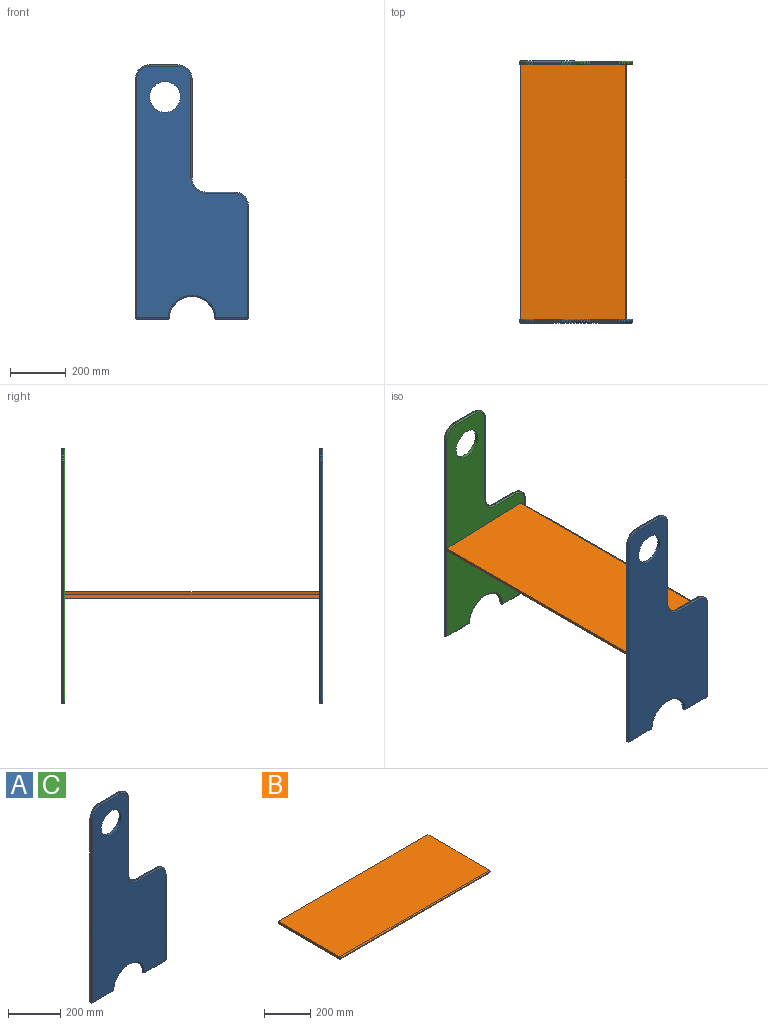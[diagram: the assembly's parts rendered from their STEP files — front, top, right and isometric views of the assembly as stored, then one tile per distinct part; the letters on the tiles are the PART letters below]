
ASSEMBLY  parts=3 mates=1
PART A: 51 faces, bbox 414.8x12.7x918.6 mm
  f0: plane 355.6x2.54mm, normal (1,0,0), area 903.2mm2, adj f10,f13,f19,f40
  f1: plane 101.6x2.54mm, normal (0,0,1), area 258.1mm2, adj f10,f11,f15,f31
  f2: plane 858.52x2.54mm, normal (-1,0,0), area 2180.6mm2, adj f11,f16,f21,f22
  f3: plane 111.61x2.54mm, normal (0,0,-1), area 283.5mm2, adj f20,f21,f29,f30
  f4: cylinder r=81.58mm len=162.87mm, axis (0,1,0), area 626.6mm2, adj f28,f29,f38,f39
  f5: plane 111.61x2.54mm, normal (0,0,-1), area 283.5mm2, adj f37,f38,f44,f45
  f6: plane 401.32x2.54mm, normal (1,0,0), area 1019.4mm2, adj f12,f36,f44,f49
  f7: plane 101.6x2.54mm, normal (0,0,1), area 258.1mm2, adj f12,f13,f27,f46
  f8: plane 904.24x396.24mm, normal (0,-1,0), area 244295.3mm2, adj f22,f26,f30,f31,f35,f39,f40,f43
  f9: plane 904.24x396.24mm, normal (0,1,0), area 244295.3mm2, adj f14,f15,f16,f17,f19,f20,f23,f27
  f10: cylinder r=50.8mm len=50.8mm, axis (0,1,0), area 202.7mm2, adj f0,f1,f17,f35
  f11: cylinder r=50.8mm len=50.8mm, axis (0,1,0), area 202.7mm2, adj f1,f2,f14,f26
  f12: cylinder r=50.8mm len=50.8mm, axis (0,1,0), area 202.7mm2, adj f6,f7,f32,f48
  f13: cylinder r=50.8mm len=50.8mm, axis (0,1,0), area 202.7mm2, adj f0,f7,f23,f43
  f14: torus R=45.72mm, axis (0,-1,0), area 613.6mm2, adj f9,f11,f15,f16
  f15: cylinder r=5.08mm len=101.6mm, axis (-1,0,0), area 810.7mm2, adj f1,f9,f14,f17
  f16: cylinder r=5.08mm len=858.52mm, axis (0,0,-1), area 6850.7mm2, adj f2,f9,f14,f18
  f17: torus R=45.72mm, axis (0,-1,0), area 613.6mm2, adj f9,f10,f15,f19
  f18: sphere r=5.08mm, area 40.5mm2, adj f16,f20,f21
  f19: cylinder r=5.08mm len=355.6mm, axis (0,0,1), area 2837.6mm2, adj f0,f9,f17,f23
  f20: cylinder r=5.08mm len=111.61mm, axis (1,0,0), area 890.6mm2, adj f3,f9,f18,f24
  f21: cylinder r=5.08mm len=5.08mm, axis (0,-1,0), area 20.3mm2, adj f2,f3,f18,f25
  f22: cylinder r=5.08mm len=858.52mm, axis (0,0,1), area 6850.7mm2, adj f2,f8,f25,f26
  f23: torus R=55.88mm, axis (0,-1,0), area 659.9mm2, adj f9,f13,f19,f27
  f24: sphere r=5.08mm, area 39mm2, adj f20,f28,f29
  f25: sphere r=5.08mm, area 40.5mm2, adj f21,f22,f30
  f26: torus R=45.72mm, axis (0,-1,0), area 613.6mm2, adj f8,f11,f22,f31
  f27: cylinder r=5.08mm len=101.6mm, axis (-1,0,0), area 810.7mm2, adj f7,f9,f23,f32
  f28: torus R=86.66mm, axis (0,-1,0), area 2013.2mm2, adj f4,f9,f24,f33
  f29: cylinder r=5.08mm len=5.07mm, axis (0,1,0), area 19.5mm2, adj f3,f4,f24,f34
  f30: cylinder r=5.08mm len=111.61mm, axis (-1,0,0), area 890.6mm2, adj f3,f8,f25,f34
  f31: cylinder r=5.08mm len=101.6mm, axis (1,0,0), area 810.7mm2, adj f1,f8,f26,f35
  f32: torus R=45.72mm, axis (0,-1,0), area 613.6mm2, adj f9,f12,f27,f36
  f33: sphere r=5.08mm, area 39mm2, adj f28,f37,f38
  f34: sphere r=5.08mm, area 39mm2, adj f29,f30,f39
  f35: torus R=45.72mm, axis (0,-1,0), area 613.6mm2, adj f8,f10,f31,f40
  f36: cylinder r=5.08mm len=401.32mm, axis (0,0,1), area 3202.4mm2, adj f6,f9,f32,f41
  f37: cylinder r=5.08mm len=111.61mm, axis (1,0,0), area 890.6mm2, adj f5,f9,f33,f41
  f38: cylinder r=5.08mm len=5.07mm, axis (0,1,0), area 19.5mm2, adj f4,f5,f33,f42
  f39: torus R=86.66mm, axis (0,-1,0), area 2013.2mm2, adj f4,f8,f34,f42
  f40: cylinder r=5.08mm len=355.6mm, axis (0,0,-1), area 2837.6mm2, adj f0,f8,f35,f43
  f41: sphere r=5.08mm, area 40.5mm2, adj f36,f37,f44
  f42: sphere r=5.08mm, area 39mm2, adj f38,f39,f45
  f43: torus R=55.88mm, axis (0,-1,0), area 659.9mm2, adj f8,f13,f40,f46
  f44: cylinder r=5.08mm len=5.08mm, axis (0,1,0), area 20.3mm2, adj f5,f6,f41,f47
  f45: cylinder r=5.08mm len=111.61mm, axis (-1,0,0), area 890.6mm2, adj f5,f8,f42,f47
  f46: cylinder r=5.08mm len=101.6mm, axis (1,0,0), area 810.7mm2, adj f7,f8,f43,f48
  f47: sphere r=5.08mm, area 40.5mm2, adj f44,f45,f49
  f48: torus R=45.72mm, axis (0,-1,0), area 613.6mm2, adj f8,f12,f46,f49
  f49: cylinder r=5.08mm len=401.32mm, axis (0,0,-1), area 3202.4mm2, adj f6,f8,f47,f48
  f50: cylinder r=55.01mm len=110.02mm, axis (0,-1,0), area 4389.6mm2, adj f8,f9
PART B: 10 faces, bbox 914.4x381x12.7 mm
  f0: plane 904.24x2.54mm, normal (0,-1,0), area 2296.8mm2, adj f6,f7,f8,f9
  f1: plane 375.92x12.7mm, normal (1,0,0), area 4774.2mm2, adj f2,f4,f5,f9
  f2: plane 914.4x12.7mm, normal (0,1,0), area 11612.9mm2, adj f1,f3,f4,f5
  f3: plane 375.92x12.7mm, normal (-1,0,0), area 4774.2mm2, adj f2,f4,f5,f6
  f4: plane 914.4x375.92mm, normal (0,0,1), area 343741.2mm2, adj f1,f2,f3,f7
  f5: plane 914.4x375.92mm, normal (0,0,-1), area 343741.2mm2, adj f1,f2,f3,f8
  f6: cylinder r=5.08mm len=12.7mm, axis (0,0,-1), area 71.9mm2, adj f0,f3,f7,f8
  f7: cylinder r=5.08mm len=914.4mm, axis (-1,0,0), area 7267.1mm2, adj f0,f4,f6,f9
  f8: cylinder r=5.08mm len=914.4mm, axis (1,0,0), area 7267.1mm2, adj f0,f5,f6,f9
  f9: cylinder r=5.08mm len=12.7mm, axis (0,0,1), area 71.9mm2, adj f0,f1,f7,f8
PART C: same geometry as A
PLACE A t=(198.12,5.08,457.2)mm
PLACE B rot(axis=(-0.02,-0.02,1),90deg) t=(190.6,462.28,382.95)mm
PLACE C t=(198.12,932.18,457.2)mm
MATE revolute B.f3 <-> A.f9  axis (0,-1,0) through (0,5.08,383.54)mm
